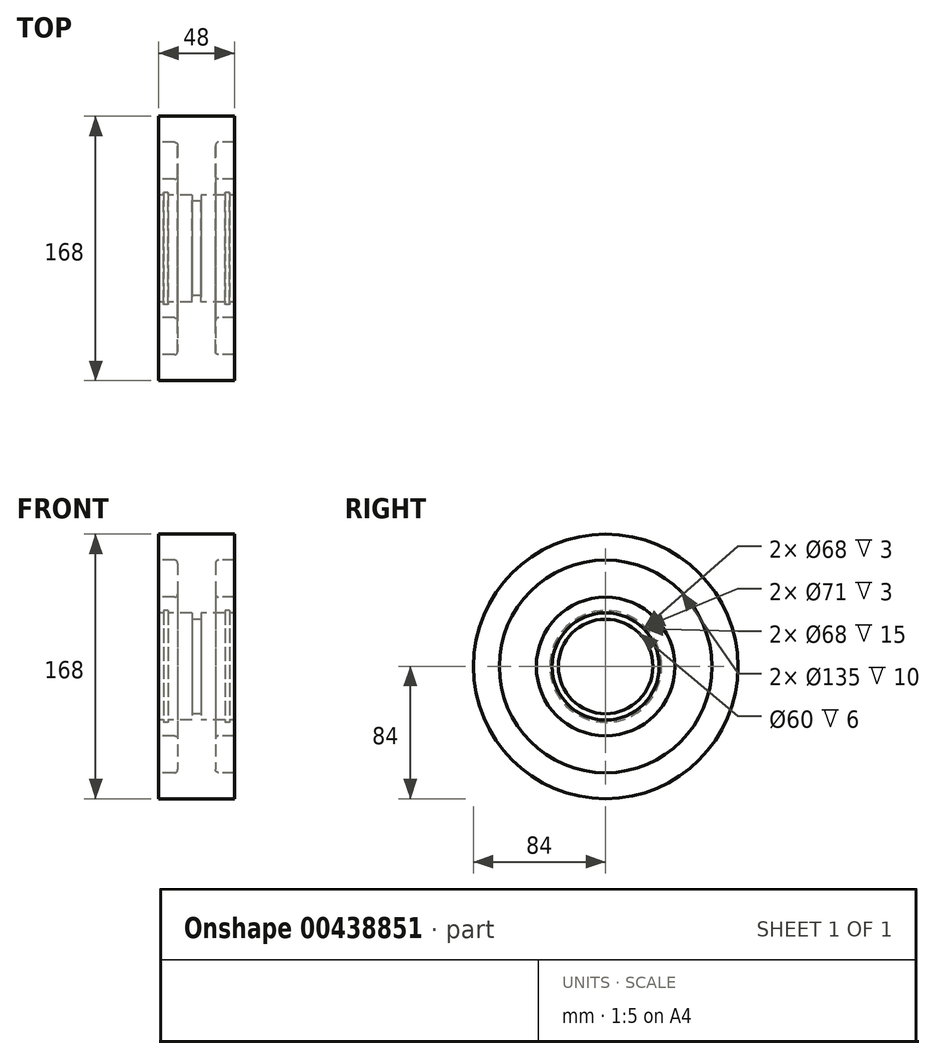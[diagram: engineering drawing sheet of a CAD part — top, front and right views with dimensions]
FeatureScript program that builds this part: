
annotation { "Feature Type Name" : "Feature", "Feature Type Description" : "" }
export const myFeature = defineFeature(function(context is Context, id is Id, definition is map)
    precondition{}
    {
        {
            var Q0;
            Q0=qCreatedBy(makeId("Front.planeOp"),FACE);
            var sketch = newSketch(context, id + "F0", { "sketchPlane" : qUnion([Q0])});
            skLineSegment(sketch, "E0", {"start": v(0, 0) * mm, "end": v(0, 84) * mm, "construction": true});
            skLineSegment(sketch, "E1", {"start": v(0, 84) * mm, "end": v(-24, 84) * mm});
            skLineSegment(sketch, "E2", {"start": v(-24, 84) * mm, "end": v(-24, 67.5) * mm});
            skLineSegment(sketch, "E3", {"start": v(-24, 0) * mm, "end": v(0, 0) * mm, "construction": true});
            skLineSegment(sketch, "E4", {"start": v(-24, 34) * mm, "end": v(-21, 34) * mm});
            skLineSegment(sketch, "E5", {"start": v(-21, 34) * mm, "end": v(-21, 35.5) * mm});
            skLineSegment(sketch, "E6", {"start": v(-21, 35.5) * mm, "end": v(-18, 35.5) * mm});
            skLineSegment(sketch, "E7", {"start": v(-18, 35.5) * mm, "end": v(-18, 34) * mm});
            skLineSegment(sketch, "E8", {"start": v(-18, 34) * mm, "end": v(-3, 34) * mm});
            skLineSegment(sketch, "E9", {"start": v(-3, 34) * mm, "end": v(-3, 30) * mm});
            skLineSegment(sketch, "E10", {"start": v(-3, 30) * mm, "end": v(0, 30) * mm});
            skLineSegment(sketch, "E11", {"start": v(-24, 44) * mm, "end": v(-14, 44) * mm});
            skLineSegment(sketch, "E12", {"start": v(-12, 46) * mm, "end": v(-12, 65.5) * mm});
            skLineSegment(sketch, "E13", {"start": v(-14, 67.5) * mm, "end": v(-24, 67.5) * mm});
            skLineSegment(sketch, "E14.trimOffspring", {"start": v(-24, 44) * mm, "end": v(-24, 34) * mm});
            skPoint(sketch, "E15.visualSharp", {"position": v(-12, 67.5) * mm});
            skArc(sketch, "E15.filletArc", {"start": v(-12, 65.5) * mm, "mid": v(-12.59, 66.91) * mm, "end": v(-14, 67.5) * mm});
            skPoint(sketch, "E16.visualSharp", {"position": v(-12, 44) * mm});
            skArc(sketch, "E16.filletArc", {"start": v(-14, 44) * mm, "mid": v(-12.59, 44.59) * mm, "end": v(-12, 46) * mm});
            skLineSegment(sketch, "E17.MirrorCS", {"start": v(0, 84) * mm, "end": v(24, 84) * mm});
            skLineSegment(sketch, "E18.MirrorCS", {"start": v(24, 84) * mm, "end": v(24, 67.5) * mm});
            skLineSegment(sketch, "E19.MirrorCS", {"start": v(14, 67.5) * mm, "end": v(24, 67.5) * mm});
            skArc(sketch, "E20.MirrorCS", {"start": v(12, 65.5) * mm, "mid": v(12.59, 66.91) * mm, "end": v(14, 67.5) * mm});
            skLineSegment(sketch, "E21.MirrorCS", {"start": v(12, 46) * mm, "end": v(12, 65.5) * mm});
            skArc(sketch, "E22.MirrorCS", {"start": v(14, 44) * mm, "mid": v(12.59, 44.59) * mm, "end": v(12, 46) * mm});
            skLineSegment(sketch, "E23.MirrorCS", {"start": v(24, 44) * mm, "end": v(14, 44) * mm});
            skLineSegment(sketch, "E24.MirrorCS", {"start": v(24, 44) * mm, "end": v(24, 34) * mm});
            skLineSegment(sketch, "E25.MirrorCS", {"start": v(24, 34) * mm, "end": v(21, 34) * mm});
            skLineSegment(sketch, "E26.MirrorCS", {"start": v(21, 35.5) * mm, "end": v(18, 35.5) * mm});
            skLineSegment(sketch, "E27.MirrorCS", {"start": v(18, 35.5) * mm, "end": v(18, 34) * mm});
            skLineSegment(sketch, "E28.MirrorCS", {"start": v(18, 34) * mm, "end": v(3, 34) * mm});
            skLineSegment(sketch, "E29.MirrorCS", {"start": v(3, 34) * mm, "end": v(3, 30) * mm});
            skLineSegment(sketch, "E30.MirrorCS", {"start": v(3, 30) * mm, "end": v(0, 30) * mm});
            skLineSegment(sketch, "E31.MirrorCS", {"start": v(21, 34) * mm, "end": v(21, 35.5) * mm});
            skSolve(sketch);
        }
        {
            var Q0;
            Q0 = qSketchRegion(id + "F0", true);
            var Q1;
            Q1=sQuery(id+"F0.wireOp",EDGE,"E3");
            revolve(context, id + "F1", {"entities" : qUnion([Q0]), "axis" : qUnion([Q1]), "revolveType" : RevolveType.FULL});
        }
    });
